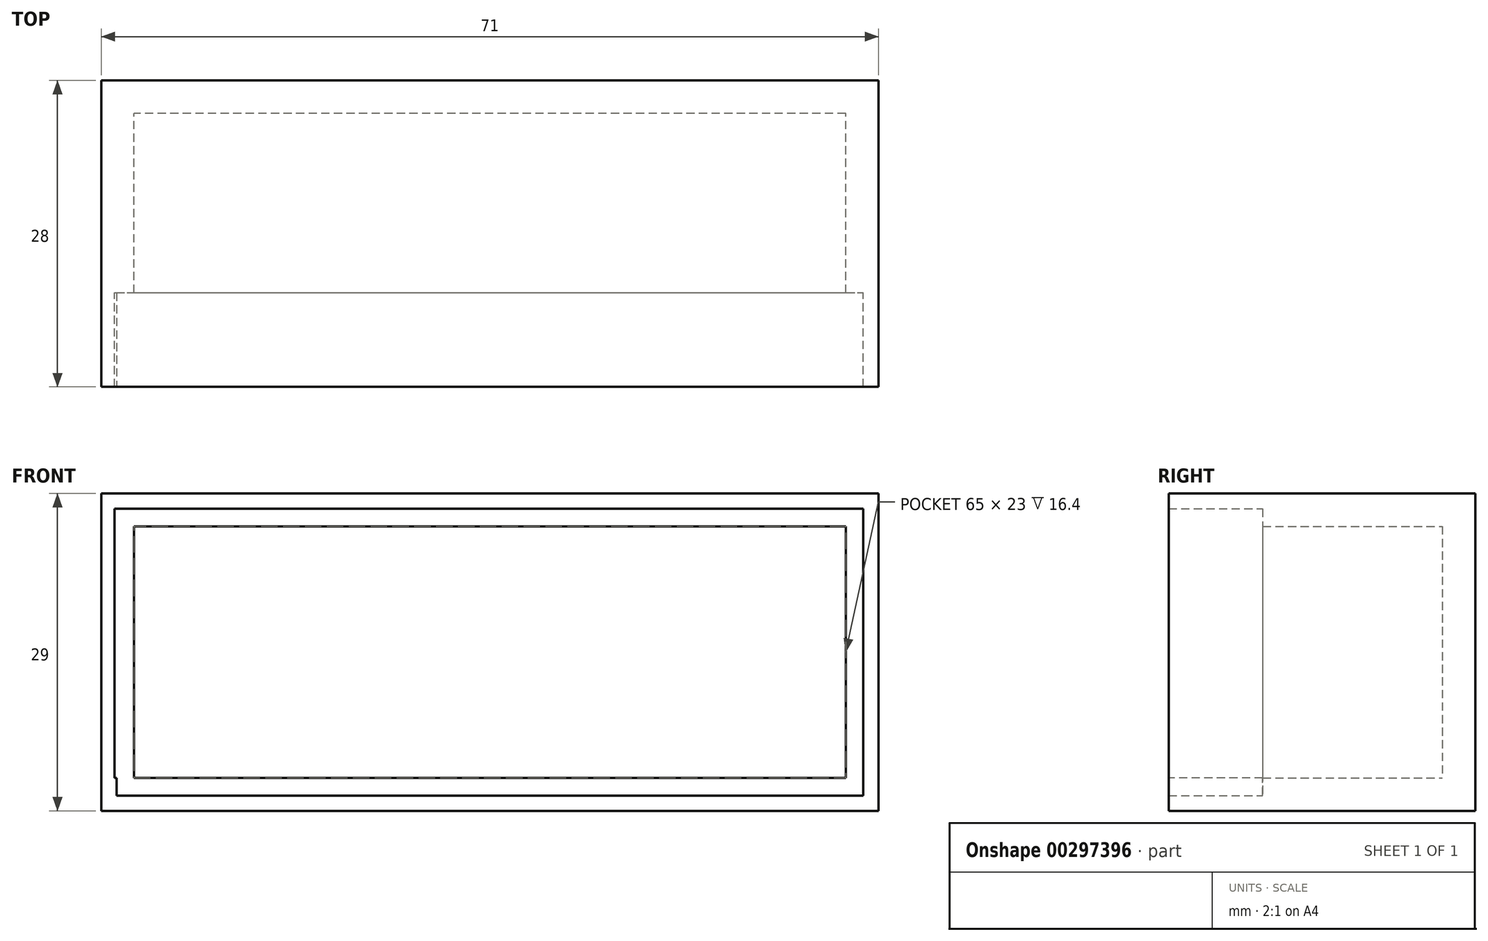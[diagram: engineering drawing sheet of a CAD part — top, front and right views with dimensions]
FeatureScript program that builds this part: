
annotation { "Feature Type Name" : "Feature", "Feature Type Description" : "" }
export const myFeature = defineFeature(function(context is Context, id is Id, definition is map)
    precondition{}
    {
        {
            var Q0;
            Q0=qCreatedBy(makeId("Top.planeOp"),FACE);
            var sketch = newSketch(context, id + "F0", { "sketchPlane" : qUnion([Q0])});
            skLineSegment(sketch, "E0.top", {"start": v(0, 25) * mm, "end": v(-65, 25) * mm});
            skLineSegment(sketch, "E0.left", {"start": v(0, 8.6) * mm, "end": v(0, 25) * mm});
            skLineSegment(sketch, "E0.right", {"start": v(-65, 8.6) * mm, "end": v(-65, 25) * mm});
            skLineSegment(sketch, "E1.0", {"start": v(3, 0) * mm, "end": v(3, 28) * mm});
            skLineSegment(sketch, "E1.1", {"start": v(3, 28) * mm, "end": v(-68, 28) * mm});
            skLineSegment(sketch, "E1.2", {"start": v(-68, 0) * mm, "end": v(-68, 28) * mm});
            skLineSegment(sketch, "E2", {"start": v(-66.8, 0) * mm, "end": v(-66.8, 8.6) * mm});
            skLineSegment(sketch, "E3", {"start": v(1.6, 0) * mm, "end": v(1.6, 8.6) * mm});
            skLineSegment(sketch, "E4", {"start": v(-66.8, 8.6) * mm, "end": v(-65, 8.6) * mm});
            skLineSegment(sketch, "E5.trimOffspring", {"start": v(0, 8.6) * mm, "end": v(1.6, 8.6) * mm});
            skLineSegment(sketch, "E6", {"start": v(-68, 0) * mm, "end": v(-66.8, 0) * mm});
            skLineSegment(sketch, "E7", {"start": v(1.6, 0) * mm, "end": v(3, 0) * mm});
            skSolve(sketch);
        }
        {
            var Q0;
            Q0=makeQuery(id+"F0.imprint","IMPRINT",FACE,{"disambiguationData":[TD([[makeQuery(id+"F0.imprint","IMPRINT",EDGE,{"derivedFrom":sQuery(id+"F0.wireOp",EDGE,"E0.top")}),-1.0]])]});
            extrude(context, id + "F1", {"entities" : qUnion([Q0]), "depth" : 23 * mm});
        }
        {
            var Q0;
            Q0=makeQuery(id+"F1.opExtrude","CAP_FACE",FACE,{"disambiguationData":[OSD([sQuery(id+"F0.wireOp",EDGE,"E0.top"),sQuery(id+"F0.wireOp",EDGE,"E0.left"),sQuery(id+"F0.wireOp",EDGE,"E0.right"),sQuery(id+"F0.wireOp",EDGE,"E1.0"),sQuery(id+"F0.wireOp",EDGE,"E1.1"),sQuery(id+"F0.wireOp",EDGE,"E1.2"),sQuery(id+"F0.wireOp",EDGE,"E2"),sQuery(id+"F0.wireOp",EDGE,"E3"),sQuery(id+"F0.wireOp",EDGE,"E4"),sQuery(id+"F0.wireOp",EDGE,"E5.trimOffspring"),sQuery(id+"F0.wireOp",EDGE,"E6"),sQuery(id+"F0.wireOp",EDGE,"E7")])],"isStart":false});
            var sketch = newSketch(context, id + "F2", { "sketchPlane" : qUnion([Q0])});
            skLineSegment(sketch, "E8.bottom", {"start": v(-68, 28) * mm, "end": v(3, 28) * mm});
            skLineSegment(sketch, "E8.top", {"start": v(-68, 0) * mm, "end": v(3, 0) * mm});
            skLineSegment(sketch, "E8.left", {"start": v(-68, 28) * mm, "end": v(-68, 0) * mm});
            skLineSegment(sketch, "E8.right", {"start": v(3, 28) * mm, "end": v(3, 0) * mm});
            skSolve(sketch);
        }
        {
            var Q0;
            Q0=makeQuery(id+"F2.imprint","IMPRINT",FACE,{"disambiguationData":[TD([[makeQuery(id+"F2.imprint","IMPRINT",EDGE,{"derivedFrom":sQuery(id+"F2.wireOp",EDGE,"E8.bottom")}),1.0]])]});
            var Q1;
            Q1=makeQuery(id+"F2.imprint","IMPRINT",FACE,{"disambiguationData":[TD([[makeQuery(id+"F2.imprint","IMPRINT",EDGE,{"derivedFrom":makeQuery(id+"F1.opExtrude","CAP_EDGE",EDGE,{"disambiguationData":[OSD([sQuery(id+"F0.wireOp",EDGE,"E0.top")])],"isStart":false})}),1.0]])]});
            extrude(context, id + "F3", {"entities" : qUnion([Q0, Q1]), "operationType" : NewBodyOperationType.ADD, "depth" : 3 * mm});
        }
        {
            var Q0;
            Q0=makeQuery(id+"F3.opExtrude","CAP_FACE",FACE,{"disambiguationData":[OSD([sQuery(id+"F2.wireOp",EDGE,"E8.bottom"),sQuery(id+"F2.wireOp",EDGE,"E8.top"),sQuery(id+"F2.wireOp",EDGE,"E8.left"),sQuery(id+"F2.wireOp",EDGE,"E8.right")])],"isStart":true});
            var sketch = newSketch(context, id + "F4", { "sketchPlane" : qUnion([Q0])});
            skLineSegment(sketch, "E9.bottom", {"start": v(-66.8, 0) * mm, "end": v(1.6, 0) * mm});
            skLineSegment(sketch, "E9.top", {"start": v(-66.8, -8.6) * mm, "end": v(1.6, -8.6) * mm});
            skLineSegment(sketch, "E9.left", {"start": v(-66.8, 0) * mm, "end": v(-66.8, -8.6) * mm});
            skLineSegment(sketch, "E9.right", {"start": v(1.6, 0) * mm, "end": v(1.6, -8.6) * mm});
            skSolve(sketch);
        }
        {
            var Q0;
            Q0=makeQuery(id+"F4.imprint","IMPRINT",FACE,{"disambiguationData":[TD([[makeQuery(id+"F4.imprint","IMPRINT",EDGE,{"derivedFrom":sQuery(id+"F4.wireOp",EDGE,"E9.bottom")}),-1.0]])]});
            extrude(context, id + "F5", {"entities" : qUnion([Q0]), "operationType" : NewBodyOperationType.REMOVE, "oppositeDirection" : true, "depth" : 1.6 * mm});
        }
        {
            var Q0;
            Q0=makeQuery(id+"F1.opExtrude","CAP_FACE",FACE,{"disambiguationData":[OSD([sQuery(id+"F0.wireOp",EDGE,"E0.top"),sQuery(id+"F0.wireOp",EDGE,"E0.left"),sQuery(id+"F0.wireOp",EDGE,"E0.right"),sQuery(id+"F0.wireOp",EDGE,"E1.0"),sQuery(id+"F0.wireOp",EDGE,"E1.1"),sQuery(id+"F0.wireOp",EDGE,"E1.2"),sQuery(id+"F0.wireOp",EDGE,"E2"),sQuery(id+"F0.wireOp",EDGE,"E3"),sQuery(id+"F0.wireOp",EDGE,"E4"),sQuery(id+"F0.wireOp",EDGE,"E5.trimOffspring"),sQuery(id+"F0.wireOp",EDGE,"E6"),sQuery(id+"F0.wireOp",EDGE,"E7")])],"isStart":true});
            var sketch = newSketch(context, id + "F6", { "sketchPlane" : qUnion([Q0])});
            skLineSegment(sketch, "E10.bottom", {"start": v(-68, 0) * mm, "end": v(3, 0) * mm});
            skLineSegment(sketch, "E10.top", {"start": v(-68, -28) * mm, "end": v(3, -28) * mm});
            skLineSegment(sketch, "E10.left", {"start": v(-68, 0) * mm, "end": v(-68, -28) * mm});
            skLineSegment(sketch, "E10.right", {"start": v(3, 0) * mm, "end": v(3, -28) * mm});
            skSolve(sketch);
        }
        {
            var Q0;
            Q0=makeQuery(id+"F6.imprint","IMPRINT",FACE,{"disambiguationData":[TD([[makeQuery(id+"F6.imprint","IMPRINT",EDGE,{"derivedFrom":sQuery(id+"F6.wireOp",EDGE,"E10.top")}),-1.0]])]});
            var Q1;
            Q1=makeQuery(id+"F6.imprint","IMPRINT",FACE,{"disambiguationData":[TD([[makeQuery(id+"F6.imprint","IMPRINT",EDGE,{"derivedFrom":makeQuery(id+"F1.opExtrude","CAP_EDGE",EDGE,{"disambiguationData":[OSD([sQuery(id+"F0.wireOp",EDGE,"E0.top")])],"isStart":true})}),-1.0]])]});
            extrude(context, id + "F7", {"entities" : qUnion([Q0, Q1]), "operationType" : NewBodyOperationType.ADD, "depth" : 3 * mm});
        }
        {
            var Q0;
            Q0=makeQuery(id+"F7.opExtrude","CAP_FACE",FACE,{"disambiguationData":[OSD([sQuery(id+"F6.wireOp",EDGE,"E10.bottom"),sQuery(id+"F6.wireOp",EDGE,"E10.top"),sQuery(id+"F6.wireOp",EDGE,"E10.left"),sQuery(id+"F6.wireOp",EDGE,"E10.right")])],"isStart":true});
            var sketch = newSketch(context, id + "F8", { "sketchPlane" : qUnion([Q0])});
            skLineSegment(sketch, "E11.bottom", {"start": v(-66.6, 8.6) * mm, "end": v(1.6, 8.6) * mm});
            skLineSegment(sketch, "E11.top", {"start": v(-66.6, 0) * mm, "end": v(1.6, 0) * mm});
            skLineSegment(sketch, "E11.left", {"start": v(-66.6, 8.6) * mm, "end": v(-66.6, 0) * mm});
            skLineSegment(sketch, "E11.right", {"start": v(1.6, 8.6) * mm, "end": v(1.6, 0) * mm});
            skSolve(sketch);
        }
        {
            var Q0;
            Q0=makeQuery(id+"F8.imprint","IMPRINT",FACE,{"disambiguationData":[TD([[makeQuery(id+"F8.imprint","IMPRINT",EDGE,{"derivedFrom":sQuery(id+"F8.wireOp",EDGE,"E11.top")}),1.0]])]});
            extrude(context, id + "F9", {"entities" : qUnion([Q0]), "operationType" : NewBodyOperationType.REMOVE, "oppositeDirection" : true, "depth" : 1.6 * mm});
        }
    });
